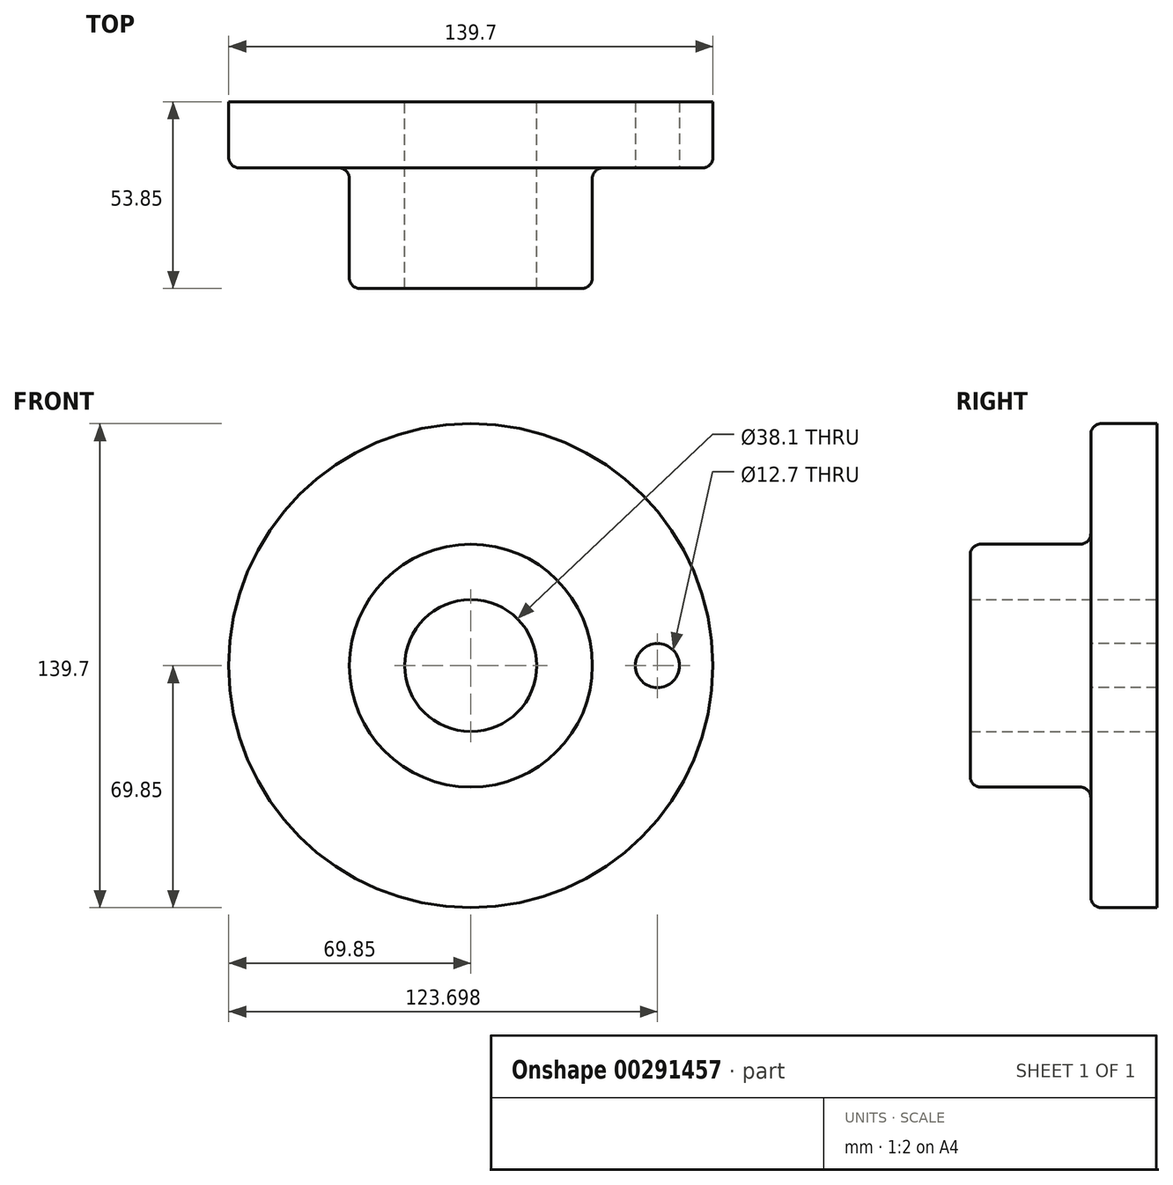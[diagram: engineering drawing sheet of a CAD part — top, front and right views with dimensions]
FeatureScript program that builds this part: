
annotation { "Feature Type Name" : "Feature", "Feature Type Description" : "" }
export const myFeature = defineFeature(function(context is Context, id is Id, definition is map)
    precondition{}
    {
        {
            var Q0;
            Q0=qCreatedBy(makeId("Right.planeOp"),FACE);
            var sketch = newSketch(context, id + "F0", { "sketchPlane" : qUnion([Q0])});
            skLineSegment(sketch, "E0", {"start": v(0, 19.05) * mm, "end": v(0, 69.85) * mm});
            skLineSegment(sketch, "E1", {"start": v(0, 69.85) * mm, "end": v(-16, 69.85) * mm});
            skLineSegment(sketch, "E2", {"start": v(-19.05, 66.8) * mm, "end": v(-19.05, 38.1) * mm});
            skLineSegment(sketch, "E3", {"start": v(-22.1, 35.05) * mm, "end": v(-50.8, 35.05) * mm});
            skLineSegment(sketch, "E4", {"start": v(-53.85, 32) * mm, "end": v(-53.85, 19.05) * mm});
            skLineSegment(sketch, "E5", {"start": v(-53.85, 19.05) * mm, "end": v(0, 19.05) * mm});
            skLineSegment(sketch, "E6", {"start": v(0, 0) * mm, "end": v(-27.14, 0) * mm});
            skPoint(sketch, "E7.visualSharp", {"position": v(-53.85, 35.05) * mm});
            skArc(sketch, "E7.filletArc", {"start": v(-50.8, 35.05) * mm, "mid": v(-52.96, 34.16) * mm, "end": v(-53.85, 32) * mm});
            skPoint(sketch, "E8.visualSharp", {"position": v(-19.05, 35.05) * mm});
            skArc(sketch, "E8.filletArc", {"start": v(-22.1, 35.05) * mm, "mid": v(-19.94, 35.94) * mm, "end": v(-19.05, 38.1) * mm});
            skPoint(sketch, "E9.visualSharp", {"position": v(-19.05, 69.85) * mm});
            skArc(sketch, "E9.filletArc", {"start": v(-16, 69.85) * mm, "mid": v(-18.16, 68.96) * mm, "end": v(-19.05, 66.8) * mm});
            skSolve(sketch);
        }
        {
            var Q0;
            Q0 = qSketchRegion(id + "F0", true);
            var Q1;
            Q1=sQuery(id+"F0.wireOp",EDGE,"E6");
            revolve(context, id + "F1", {"entities" : qUnion([Q0]), "axis" : qUnion([Q1]), "revolveType" : RevolveType.FULL});
        }
        {
            var Q0;
            Q0=makeQuery(id+"F1.opRevolve","SWEPT_FACE",FACE,{"disambiguationData":[OSD([sQuery(id+"F0.wireOp",EDGE,"E2")])]});
            var sketch = newSketch(context, id + "F2", { "sketchPlane" : qUnion([Q0])});
            skCircle(sketch, "E10", {"center": v(0, 0) * mm, "radius": 53.85 * mm});
            skCircle(sketch, "E11", {"center": v(53.85, 0) * mm, "radius": 6.35 * mm});
            skSolve(sketch);
        }
        {
            var Q0;
            {var subQ0=sQuery(id+"F2.wireOp",EDGE,"E11");var subQ1=sQuery(id+"F2.wireOp",EDGE,"E10");var subQ2=makeQuery(id+"F2.imprint","INTERSECT",VERTEX,{"disambiguationData":[OD(0.0)],"derivedFrom":[subQ1,subQ0]});Q0=makeQuery(id+"F2.imprint","IMPRINT",FACE,{"disambiguationData":[TD([[makeQuery(id+"F2.imprint","IMPRINT",EDGE,{"disambiguationData":[TD([[subQ2,-1.0]])],"derivedFrom":subQ1}),1.0]])]});}
            var Q1;
            {var subQ0=sQuery(id+"F2.wireOp",EDGE,"E11");var subQ1=sQuery(id+"F2.wireOp",EDGE,"E10");var subQ2=makeQuery(id+"F2.imprint","INTERSECT",VERTEX,{"disambiguationData":[OD(0.0)],"derivedFrom":[subQ1,subQ0]});Q1=makeQuery(id+"F2.imprint","IMPRINT",FACE,{"disambiguationData":[TD([[makeQuery(id+"F2.imprint","IMPRINT",EDGE,{"disambiguationData":[TD([[subQ2,-1.0]])],"derivedFrom":subQ1}),-1.0]])]});}
            extrude(context, id + "F3", {"entities" : qUnion([Q0, Q1]), "operationType" : NewBodyOperationType.REMOVE, "oppositeDirection" : true, "depth" : 25.4 * mm});
        }
    });
